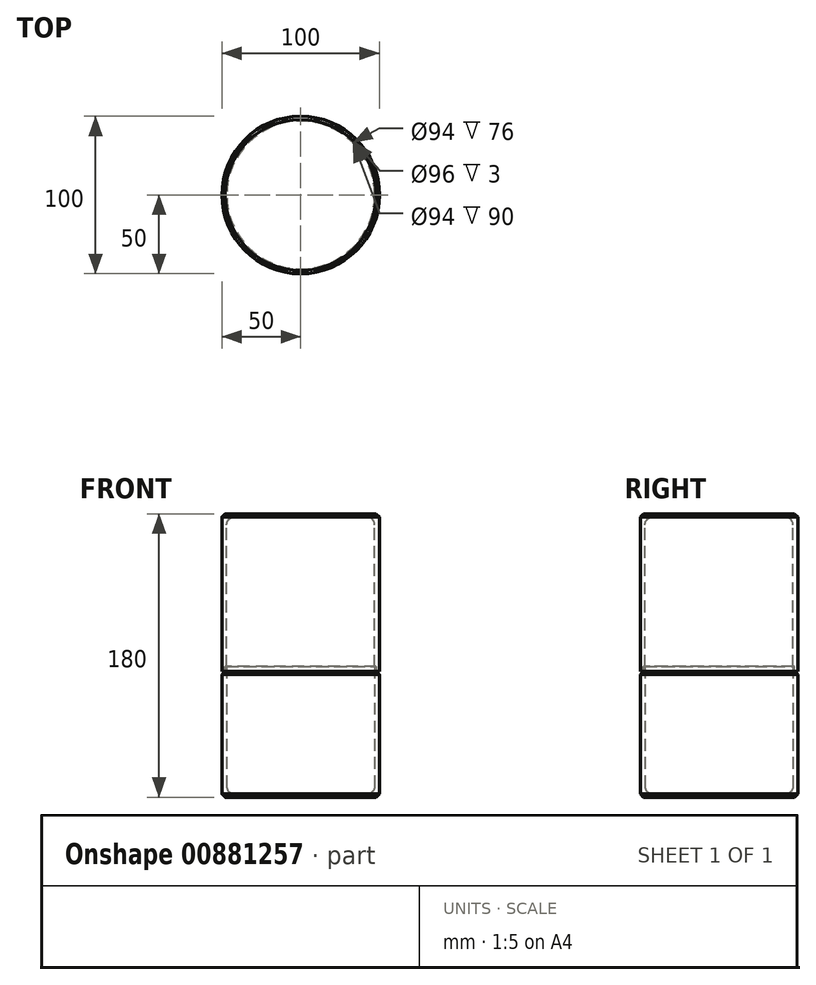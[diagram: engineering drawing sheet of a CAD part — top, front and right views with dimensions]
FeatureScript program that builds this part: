
annotation { "Feature Type Name" : "Feature", "Feature Type Description" : "" }
export const myFeature = defineFeature(function(context is Context, id is Id, definition is map)
    precondition{}
    {
        {
            var Q0;
            Q0=qCreatedBy(makeId("Front.planeOp"),FACE);
            var sketch = newSketch(context, id + "F0", { "sketchPlane" : qUnion([Q0])});
            skLineSegment(sketch, "E0", {"start": v(-50, 130) * mm, "end": v(-50, 30) * mm});
            skLineSegment(sketch, "E1", {"start": v(-50, 30) * mm, "end": v(-48, 30) * mm});
            skLineSegment(sketch, "E2", {"start": v(-48, 30) * mm, "end": v(-48, 33) * mm});
            skLineSegment(sketch, "E3", {"start": v(-48, 33) * mm, "end": v(-47, 33) * mm});
            skLineSegment(sketch, "E4", {"start": v(-47, 33) * mm, "end": v(-47, 130) * mm});
            skLineSegment(sketch, "E5", {"start": v(-47, 130) * mm, "end": v(-50, 130) * mm});
            skLineSegment(sketch, "E6", {"start": v(-47, 130) * mm, "end": v(0, 130) * mm});
            skLineSegment(sketch, "E7", {"start": v(0, 130) * mm, "end": v(0, 128) * mm});
            skLineSegment(sketch, "E8", {"start": v(0, 128) * mm, "end": v(-50, 128) * mm});
            skSolve(sketch);
        }
        {
            var Q0;
            Q0 = qSketchRegion(id + "F0", true);
            var Q1;
            Q1=sQuery(id+"F0.wireOp",EDGE,"E7");
            revolve(context, id + "F1", {"surfaceOperationType" : NewSurfaceOperationType.NEW, "entities" : qUnion([Q0]), "axis" : qUnion([Q1]), "revolveType" : RevolveType.FULL});
        }
        {
            var Q0;
            Q0=qCreatedBy(makeId("Front.planeOp"),FACE);
            var sketch = newSketch(context, id + "F2", { "sketchPlane" : qUnion([Q0])});
            skLineSegment(sketch, "E9.0", {"start": v(-47.7, 30) * mm, "end": v(-47.7, 33) * mm});
            skLineSegment(sketch, "E10.0", {"start": v(-50, 30) * mm, "end": v(-47.7, 30) * mm});
            skLineSegment(sketch, "E11.0", {"start": v(-48, 33) * mm, "end": v(-47, 33) * mm});
            skLineSegment(sketch, "E12", {"start": v(-50, -50) * mm, "end": v(-50, 30) * mm});
            skLineSegment(sketch, "E13", {"start": v(-47.7, 30) * mm, "end": v(-50, 30) * mm});
            skLineSegment(sketch, "E14", {"start": v(-47, 33) * mm, "end": v(-47, -48) * mm});
            skLineSegment(sketch, "E15", {"start": v(-47, -50) * mm, "end": v(-50, -50) * mm});
            skLineSegment(sketch, "E16", {"start": v(-47.7, 33) * mm, "end": v(-47, 33) * mm});
            skLineSegment(sketch, "E17", {"start": v(-50, -50) * mm, "end": v(0, -50) * mm});
            skLineSegment(sketch, "E18", {"start": v(0, -50) * mm, "end": v(0, -48) * mm});
            skLineSegment(sketch, "E19", {"start": v(0, -48) * mm, "end": v(-47, -48) * mm});
            skSolve(sketch);
        }
        {
            var Q0;
            {var subQ5=sQuery(id+"F2.wireOp",EDGE,"E12");Q0=makeQuery(id+"F2.imprint","IMPRINT",FACE,{"disambiguationData":[TD([[makeQuery(id+"F2.imprint","IMPRINT",EDGE,{"derivedFrom":subQ5}),-1.0]])]});}
            var Q1;
            Q1=sQuery(id+"F2.wireOp",EDGE,"E18");
            revolve(context, id + "F3", {"surfaceOperationType" : NewSurfaceOperationType.NEW, "entities" : qUnion([Q0]), "axis" : qUnion([Q1]), "revolveType" : RevolveType.FULL});
        }
        {
            var Q0;
            Q0=makeQuery(id+"F3.opRevolve","SWEPT_EDGE",EDGE,{"disambiguationData":[OSD([sQuery(id+"F2.wireOp",EDGE,"E12"),sQuery(id+"F2.wireOp",EDGE,"E17")])]});
            chamfer(context, id + "F4", {"entities" : qUnion([Q0]), "width" : 2 * mm, "tangentPropagation" : true});
        }
        {
            var Q0;
            Q0=makeQuery(id+"F3.opRevolve","SWEPT_EDGE",EDGE,{"disambiguationData":[OSD([sQuery(id+"F2.wireOp",EDGE,"E14"),sQuery(id+"F2.wireOp",EDGE,"E19")])]});
            fillet(context, id + "F5", {"entities" : qUnion([Q0]), "radius" : 5 * mm, "tangentPropagation" : true, "allowEdgeOverflow" : false});
        }
        {
            var Q0;
            Q0=makeQuery(id+"F1.opRevolve","SWEPT_EDGE",EDGE,{"disambiguationData":[OSD([sQuery(id+"F0.wireOp",EDGE,"E0"),sQuery(id+"F0.wireOp",EDGE,"E5")])]});
            chamfer(context, id + "F6", {"entities" : qUnion([Q0]), "width" : 2 * mm, "tangentPropagation" : true});
        }
        {
            var Q0;
            Q0=makeQuery(id+"F1.opRevolve","SWEPT_FACE",FACE,{"disambiguationData":[OSD([sQuery(id+"F0.wireOp",EDGE,"E8")])]});
            fillet(context, id + "F7", {"entities" : qUnion([Q0]), "radius" : 5 * mm, "tangentPropagation" : true, "allowEdgeOverflow" : false});
        }
    });
